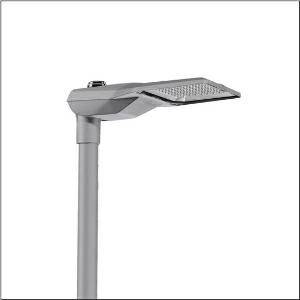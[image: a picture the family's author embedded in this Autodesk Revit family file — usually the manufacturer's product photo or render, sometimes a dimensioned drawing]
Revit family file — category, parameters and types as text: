
# Revit family: streetlight_sl_21_midi___st1_5a_5xe7p47n08lb_54ff
name_source: partatom
category: Lighting Fixtures
units: mm (PartAtom-declared; Revit-internal decimal feet)

## family parameters
Cut with Voids When Loaded = No
Host = Face
Light Source = No
Part Type = Normal
Room Calculation Point = No
Round Connector Dimension = Use Diameter
Shared = No

## types (1)
- --- (1 x LED, 14690 lm, 98.3 W, 4000K)
    Apparent Load = 98 VA
    CIE Flux Codes = 22 53 95 100 100
    Color Rendering = 70
    Color Temperature = 4000K
    Default Elevation = 1800 mm
    Description = Streetlight SL 21 midi, mast luminaire, primary light control with lens, of PMMA, primary optical cover: cover, of toughened safety glass, transparent, light distribution: ST1.5a, light emission: direct distribution, primary light characteristic: asymmetric, installation type: side-entry, LED, 3G 2.5mm², High Power LED, rated luminous flux: 14.690lm, luminous efficacy: 149lm/W, light colour: 740, colour temperature: 4000K, control: overheat protection, presetting dimming linear, constant luminous flux control, time-dependent luminous flux control, flexible luminous flux parameterisation, mains connection: 220..240V, AC, 50/60Hz, connection cable pre-assembled, cable length: 10,5m, wiring characteristics: H05VV-F, start of lifetime: 98W, end of service life: 101W, reduction: 45W, luminaire housing, of diecast aluminium (EN AC-44300), powder-coated, Siteco® metallic grey (DB 702S), corrosivity category C5 mid according to DIN EN ISO 12944, multi-level sealing system, sealing non-destructively replaceable, inclination adjustable: 0°, 5°, 10°, 15°, length: 644mm, width: 335mm, height: 110mm, spigot size: 42mm (side-entry), protection rating (complete): IP66, insulation class (complete): insulation class I (protective earthing), certification: CE, ENEC, ENEC+, VDE, impact resistance: IK09, permissible operating ambient temperature for outdoor applications: -40..+50°C, standard-compliant lighting for roads and squares, packaging unit: 1 piece

Light Distribution: ST1.5a
    Height = 111 mm
    Lamp = 1 x LED
    Lamp Light Flux = 14690 lm
    Lamp Power = 98.3 W
    Lamp count = 1
    Length = 644 mm
    Luminous efficacy = 149 lm/W
    Manufacturer = Siteco
    ModVariant = No
    Model = 5XE7P47N08LB
    Number of Poles = 1
    OnlyDefault = Yes
    Power Factor = 1
    Product Name = Streetlight SL 21 midi | ST1.5a
    Product group = mast luminaire | pylon top
    ProductGroupID = 6100
    Protection Class = Protection class I
    Protection Degree = IP 66
    RLX_Detail_Level = 1
    RLX_Emergency_Light_Flux = 0 lm
    RLX_Emergency_Type = 0
    RLX_Emergency_Type_DB = No
    RlxData = <blob elided: 93897 chars, md5=c12f1893>
    Socket = socket
    Standby Power = 0 W
    System Light Flux = 14690 lm
    System Power = 98 W
    Type Comments = factory setting: luminous flux: 100 % | dim-lin: 254 | 1020 mA
    Type Image = l_1294377.jpg
    URL = http://relux.com
    VarID = @adj_064755
    Voltage = 0 V
    Weight = 0.00 kg
    Width = 336 mm

## geometry (parser evidence)
native form markers: Blend x4, Sweep x8
no freeform markers — native parametric forms only
